# Revit family: Deca_Cuba de apoio sobrepor retangular com mesa_Cubas Espec._L.98
name_source: partatom
category: Plumbing Fixtures
units: mm (PartAtom-declared; Revit-internal decimal feet)

## family parameters
Cut with Voids When Loaded = No
Host = Face
Part Type = Normal
Room Calculation Point = No
Round Connector Dimension = Use Radius
Shared = No

## types (2) — shared parameters
Aprovado por = quattroD
Atendimento ao Cliente = 0800-0117073
Categoria = Cubas
Composição Básica = Argila; feldspato; caulim; vidrados e corantes inorgânicos.
Criado por = quattroD
Código Pai = L.98
Linha = Cubas Espec.
Manufacturer = DECA
Norma = NBR-16728-1;NBR-16728-2
Peso Líquido (Kg) = 20567
Saída de Esgoto = Válvula Curta
Segmento = Banheiro Luxo (D43)
URL = www.deca.com.br
zero-valued in all types: Default Elevation, Diâmetro Ponto de Esgoto, Raio Ponto de Esgoto

## per-type parameters (varying)
| type | Consumo | Cor Principal | Material | Model | Tipo de dispositivo economizador | Tipo de mecanismo utilizado | Tipo de rosca de entrada |
| L.98.17_Branco |  | Branco | Deca_Branco | L.98.17 |  |  |  |
| L.98.95_Ébano | Otimização do jato de água | Ébano | Deca_Ébano | L.98.95 | Sim | MVC -1/4 volta | BSP NBR 8133 |

## geometry (parser evidence)
native form markers: Sweep x2
no freeform markers — native parametric forms only
